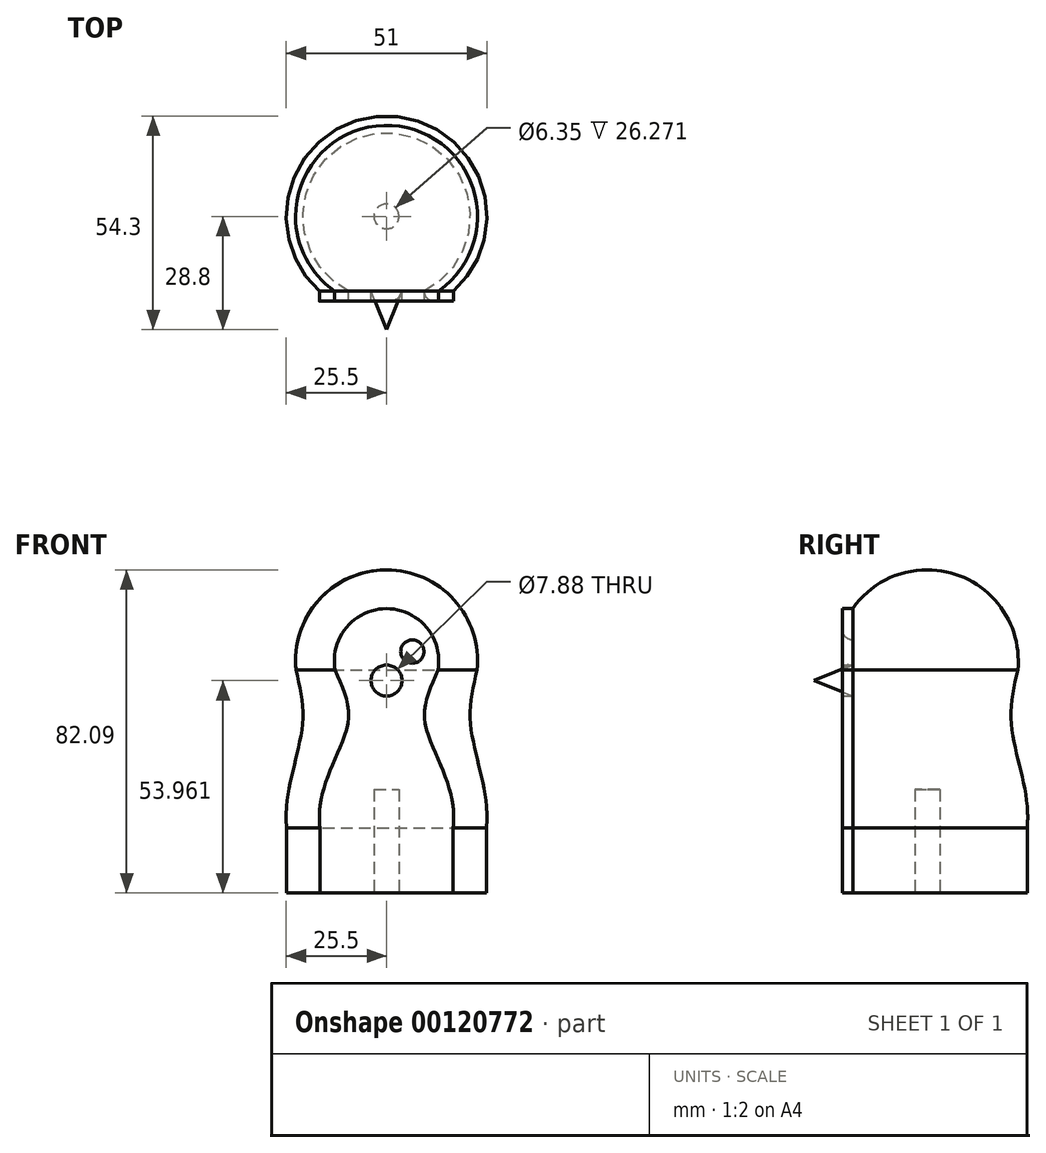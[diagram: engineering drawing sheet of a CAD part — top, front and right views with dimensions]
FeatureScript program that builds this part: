
annotation { "Feature Type Name" : "Feature", "Feature Type Description" : "" }
export const myFeature = defineFeature(function(context is Context, id is Id, definition is map)
    precondition{}
    {
        {
            var Q0;
            Q0=qCreatedBy(makeId("Front.planeOp"),FACE);
            var sketch = newSketch(context, id + "F0", { "sketchPlane" : qUnion([Q0])});
            skLineSegment(sketch, "E0", {"start": v(0, 0) * mm, "end": v(-44.47, 0) * mm});
            skFitSpline(sketch, "E1", {"points": [v(-44.47, 0) * mm, v(-49.12, 36.1) * mm, v(-41.3, 76.56) * mm, v(-44.47, 103.09) * mm], "startDerivative": vector(-23.18, 103.05) * mm, "endDerivative": vector(-19.66, 84.12) * mm});
            skArc(sketch, "E2", {"start": v(0, 152.4) * mm, "mid": v(-33.2, 137.63) * mm, "end": v(-44.47, 103.09) * mm});
            skLineSegment(sketch, "E3", {"start": v(0, 0) * mm, "end": v(0, 152.4) * mm});
            skPoint(sketch, "E4.orphan", {"position": v(44.47, 103.09) * mm});
            skLineSegment(sketch, "E5", {"start": v(-44.47, 103.09) * mm, "end": v(-44.47, 0) * mm, "construction": true});
            skPoint(sketch, "E6", {"position": v(-44.47, 59.82) * mm});
            skPoint(sketch, "E7", {"position": v(-41.15, 83.36) * mm});
            skPoint(sketch, "E8", {"position": v(-49.02, 24.5) * mm});
            skLineSegment(sketch, "E9.left", {"start": v(-44.47, 0) * mm, "end": v(-44.47, -6.35) * mm});
            skFitSpline(sketch, "E10.0", {"points": [v(-38.27, 1.4) * mm, v(-38.76, 3.56) * mm, v(-39.75, 7.85) * mm, v(-41.11, 14.14) * mm, v(-42.2, 20.33) * mm, v(-42.78, 25.45) * mm, v(-42.98, 29.55) * mm, v(-42.97, 32.11) * mm, v(-42.89, 34.18) * mm, v(-42.78, 35.73) * mm, v(-42.63, 37.3) * mm, v(-42.37, 39.44) * mm, v(-41.94, 42.18) * mm, v(-41.08, 46.69) * mm, v(-39.74, 52.48) * mm, v(-37.97, 59.57) * mm, v(-36.6, 65.52) * mm, v(-35.7, 70.27) * mm, v(-35.27, 73.23) * mm, v(-35, 75.6) * mm, v(-34.82, 77.96) * mm, v(-34.72, 80.84) * mm, v(-34.8, 84.17) * mm, v(-35.04, 87.38) * mm, v(-35.4, 90.49) * mm, v(-36.04, 94.48) * mm, v(-37.03, 99.23) * mm, v(-37.88, 102.8) * mm, v(-38.28, 104.53) * mm]});
            skArc(sketch, "E10.1", {"start": v(0, 146.05) * mm, "mid": v(-28.35, 133.52) * mm, "end": v(-38.19, 104.13) * mm});
            skLineSegment(sketch, "E11", {"start": v(-44.47, -6.35) * mm, "end": v(-6.14, -6.35) * mm});
            skLineSegment(sketch, "E12", {"start": v(-6.14, -6.35) * mm, "end": v(0, -6.35) * mm, "construction": true});
            skLineSegment(sketch, "E13", {"start": v(-6.14, -6.35) * mm, "end": v(-6.14, 0) * mm});
            skLineSegment(sketch, "E14", {"start": v(-38.27, 1.4) * mm, "end": v(-38.27, 0) * mm});
            skLineSegment(sketch, "E15", {"start": v(-49.12, 36.1) * mm, "end": v(-49.12, 0) * mm});
            skLineSegment(sketch, "E16", {"start": v(-49.12, 0) * mm, "end": v(-49.12, -6.35) * mm});
            skLineSegment(sketch, "E17", {"start": v(-49.12, -6.35) * mm, "end": v(-44.47, -6.35) * mm});
            skSolve(sketch);
        }
        {
            var Q0;
            Q0=qSketchRegion(id+"F0",true);
            var Q1;
            Q1=sQuery(id+"F0.wireOp",EDGE,"E3");
            revolve(context, id + "F1", {"entities" : qUnion([Q0]), "axis" : qUnion([Q1]), "revolveType" : RevolveType.FULL});
        }
        {
            var Q0;
            Q0=qCreatedBy(makeId("Top.planeOp"),FACE);
            var sketch = newSketch(context, id + "F2", { "sketchPlane" : qUnion([Q0])});
            skCircle(sketch, "E18", {"center": v(0, 0) * mm, "radius": 44.7 * mm, "construction": true});
            skCircle(sketch, "E19.0", {"center": v(0, 0) * mm, "radius": 44.47 * mm, "construction": true});
            skLineSegment(sketch, "E20", {"start": v(0, 0) * mm, "end": v(0, -44.47) * mm, "construction": true});
            skLineSegment(sketch, "E21", {"start": v(-25.2, -36.64) * mm, "end": v(25.6, -36.64) * mm});
            skLineSegment(sketch, "E22", {"start": v(-25.2, -36.64) * mm, "end": v(-46.78, -36.64) * mm});
            skLineSegment(sketch, "E23.bottom", {"start": v(-46.78, -36.64) * mm, "end": v(42.12, -36.64) * mm});
            skLineSegment(sketch, "E23.top", {"start": v(-46.78, -67.12) * mm, "end": v(42.12, -67.12) * mm});
            skLineSegment(sketch, "E23.left", {"start": v(-46.78, -36.64) * mm, "end": v(-46.78, -67.12) * mm});
            skLineSegment(sketch, "E23.right", {"start": v(42.12, -36.64) * mm, "end": v(42.12, -67.12) * mm});
            skSolve(sketch);
        }
        {
            var Q0;
            Q0=qSketchRegion(id+"F2",true);
            extrude(context, id + "F3", {"entities" : qUnion([Q0]), "operationType" : NewBodyOperationType.REMOVE, "depth" : 177.8 * mm, "hasSecondDirection" : true, "secondDirectionOppositeDirection" : true, "secondDirectionDepth" : 12.7 * mm});
        }
        {
            var Q0;
            Q0=makeQuery(id+"F3.boolean.opBoolean","COPY",FACE,{"derivedFrom":makeQuery(id+"F3.opExtrude","SWEPT_FACE",FACE,{"disambiguationData":[OSD([sQuery(id+"F2.wireOp",EDGE,"E23.bottom")])]})});
            var sketch = newSketch(context, id + "F4", { "sketchPlane" : qUnion([Q0])});
            skLineSegment(sketch, "E24", {"start": v(0, 0) * mm, "end": v(0, 133.3) * mm, "construction": true});
            skPoint(sketch, "E25", {"position": v(0, 112.22) * mm});
            skLineSegment(sketch, "E26", {"start": v(-12.7, 112.22) * mm, "end": v(12.7, 112.22) * mm, "construction": true});
            skCircle(sketch, "E27", {"center": v(-12.7, 112.22) * mm, "radius": 5.72 * mm});
            skCircle(sketch, "E28", {"center": v(0, 98) * mm, "radius": 7.62 * mm});
            skCircle(sketch, "E29.MirrorC", {"center": v(12.7, 112.22) * mm, "radius": 5.72 * mm});
            skLineSegment(sketch, "E30", {"start": v(-12.7, 106.5) * mm, "end": v(-12.7, 112.22) * mm, "construction": true});
            skLineSegment(sketch, "E31", {"start": v(-12.7, 112.22) * mm, "end": v(-12.7, 117.94) * mm, "construction": true});
            skSolve(sketch);
        }
        {
            var Q0;
            Q0=makeQuery(id+"F4.imprint","IMPRINT",FACE,{"disambiguationData":[TD([[makeQuery(id+"F4.imprint","IMPRINT",EDGE,{"derivedFrom":sQuery(id+"F4.wireOp",EDGE,"E28")}),1.0]])]});
            extrude(context, id + "F5", {"entities" : qUnion([Q0]), "operationType" : NewBodyOperationType.ADD, "depth" : 19.05 * mm});
        }
        {
            var Q0;
            Q0=makeQuery(id+"F5.opExtrude","CAP_EDGE",EDGE,{"disambiguationData":[OSD([sQuery(id+"F4.wireOp",EDGE,"E28")])],"isStart":false});
            chamfer(context, id + "F6", {"entities" : qUnion([Q0]), "chamferType" : ChamferType.OFFSET_ANGLE, "width" : 7.62 * mm, "oppositeDirection" : false, "angle" : 68 * degree, "tangentPropagation" : true});
        }
        {
            var Q0;
            Q0=makeQuery(id+"F4.imprint","IMPRINT",FACE,{"disambiguationData":[TD([[makeQuery(id+"F4.imprint","IMPRINT",EDGE,{"derivedFrom":sQuery(id+"F4.wireOp",EDGE,"E27")}),1.0]])]});
            var Q1;
            Q1=makeQuery(id+"F4.imprint","IMPRINT",FACE,{"disambiguationData":[TD([[makeQuery(id+"F4.imprint","IMPRINT",EDGE,{"derivedFrom":sQuery(id+"F4.wireOp",EDGE,"E29.MirrorC")}),-1.0]])]});
            extrude(context, id + "F7", {"entities" : qUnion([Q0, Q1]), "operationType" : NewBodyOperationType.ADD, "depth" : 5.08 * mm});
        }
        {
            var Q0;
            Q0=makeQuery(id+"F7.opExtrude","CAP_EDGE",EDGE,{"disambiguationData":[OSD([sQuery(id+"F4.wireOp",EDGE,"E27")])],"isStart":false});
            var Q1;
            Q1=makeQuery(id+"F7.opExtrude","CAP_EDGE",EDGE,{"disambiguationData":[OSD([sQuery(id+"F4.wireOp",EDGE,"E29.MirrorC")])],"isStart":false});
            fillet(context, id + "F8", {"entities" : qUnion([Q0, Q1]), "radius" : 5.08 * mm, "tangentPropagation" : true, "allowEdgeOverflow" : false});
        }
        {
            var Q0;
            Q0=makeQuery(id+"F1.opRevolve","SWEPT_FACE",FACE,{"disambiguationData":[OSD([sQuery(id+"F0.wireOp",EDGE,"E11"),sQuery(id+"F0.wireOp",EDGE,"E17")])]});
            var sketch = newSketch(context, id + "F9", { "sketchPlane" : qUnion([Q0])});
            skCircle(sketch, "E32.0", {"center": v(0, 0) * mm, "radius": 6.14 * mm});
            skSolve(sketch);
        }
        {
            var Q0;
            Q0=qSketchRegion(id+"F9",true);
            extrude(context, id + "F10", {"entities" : qUnion([Q0]), "operationType" : NewBodyOperationType.REMOVE, "oppositeDirection" : true, "depth" : 50.8 * mm});
        }
        {
            var Q0;
            Q0=makeQuery(id+"F1.opRevolve","SWEPT_BODY",BODY,{"disambiguationData":[OSD([sQuery(id+"F0.wireOp",EDGE,"E0"),sQuery(id+"F0.wireOp",EDGE,"E1"),sQuery(id+"F0.wireOp",EDGE,"E2"),sQuery(id+"F0.wireOp",EDGE,"E3"),sQuery(id+"F0.wireOp",EDGE,"E11"),sQuery(id+"F0.wireOp",EDGE,"E13"),sQuery(id+"F0.wireOp",EDGE,"E15"),sQuery(id+"F0.wireOp",EDGE,"E16"),sQuery(id+"F0.wireOp",EDGE,"E17")])]});
            var Q1;
            Q1=qCreatedBy(makeId("Origin.pointOp"),VERTEX);
            transform(context, id + "F11", {"entities" : qUnion([Q0]), "transformType" : TransformType.SCALE_UNIFORMLY, "scale" : .51715159, "scalePoint" : qUnion([Q1]), "makeCopy" : false});
        }
    });
